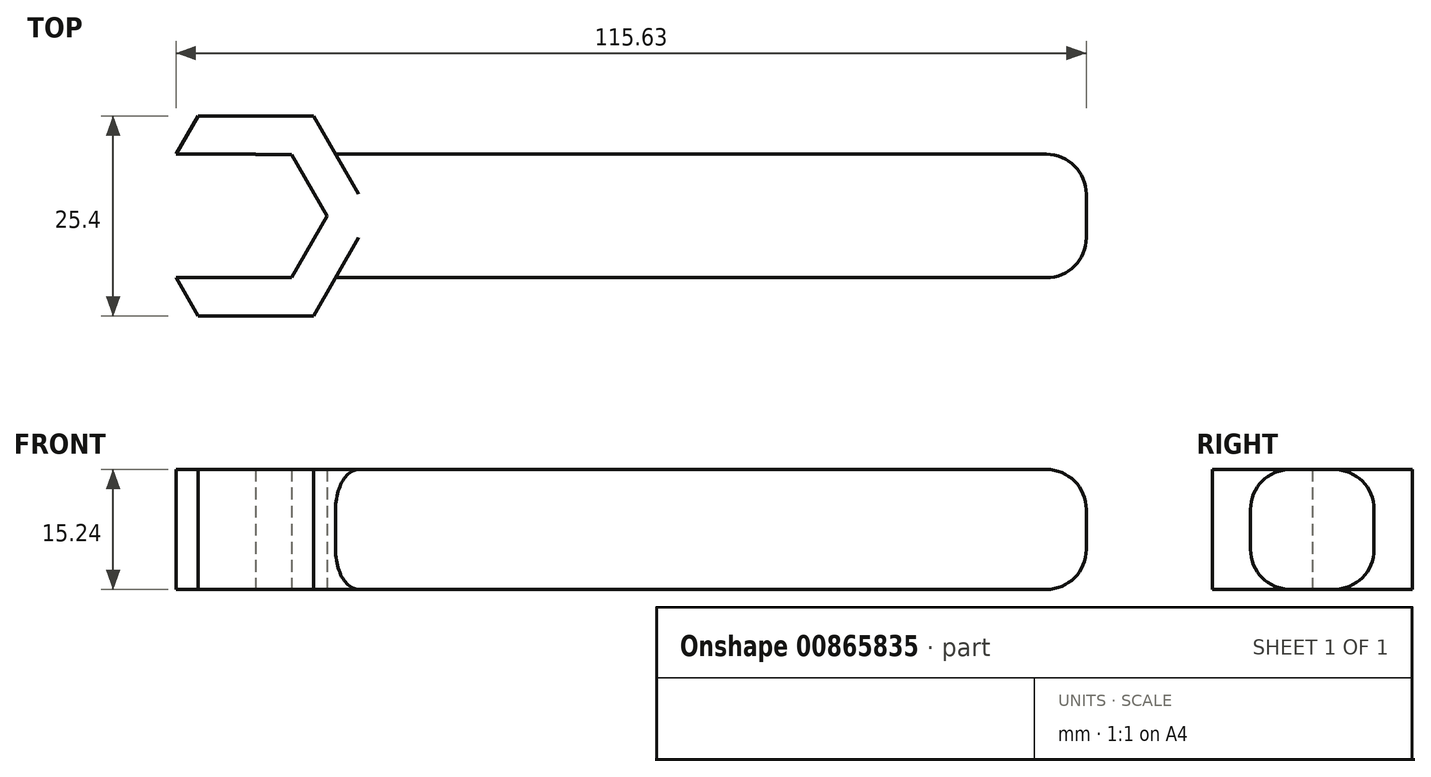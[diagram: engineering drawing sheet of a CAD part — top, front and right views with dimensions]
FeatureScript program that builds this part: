
annotation { "Feature Type Name" : "Feature", "Feature Type Description" : "" }
export const myFeature = defineFeature(function(context is Context, id is Id, definition is map)
    precondition{}
    {
        {
            var Q0;
            Q0=qCreatedBy(makeId("Top.planeOp"),FACE);
            var sketch = newSketch(context, id + "F0", { "sketchPlane" : qUnion([Q0])});
            skLineSegment(sketch, "E0.bottom", {"start": v(-35.06, 20.53) * mm, "end": v(70.43, 20.53) * mm});
            skLineSegment(sketch, "E0.top", {"start": v(-35.06, 4.85) * mm, "end": v(70.43, 4.85) * mm});
            skLineSegment(sketch, "E0.left", {"start": v(-35.06, 20.53) * mm, "end": v(-35.06, 4.85) * mm});
            skLineSegment(sketch, "E0.right", {"start": v(70.43, 20.53) * mm, "end": v(70.43, 4.85) * mm});
            skCircle(sketch, "E1.cCircle", {"center": v(-35.06, 12.69) * mm, "radius": 12.7 * mm, "construction": true});
            skLineSegment(sketch, "E1.0", {"start": v(-20.4, 12.69) * mm, "end": v(-27.73, 0) * mm});
            skLineSegment(sketch, "E1.1", {"start": v(-27.73, 0) * mm, "end": v(-42.4, 0) * mm});
            skLineSegment(sketch, "E1.2", {"start": v(-42.4, 0) * mm, "end": v(-49.73, 12.69) * mm});
            skLineSegment(sketch, "E1.3", {"start": v(-49.73, 12.69) * mm, "end": v(-42.4, 25.39) * mm});
            skLineSegment(sketch, "E1.4", {"start": v(-42.4, 25.39) * mm, "end": v(-27.73, 25.39) * mm});
            skLineSegment(sketch, "E1.5", {"start": v(-27.73, 25.39) * mm, "end": v(-20.4, 12.69) * mm});
            skPoint(sketch, "E1.0.midPoint", {"position": v(-24.07, 6.34) * mm});
            skCircle(sketch, "E2.cCircle", {"center": v(-35.06, 12.69) * mm, "radius": 7.83 * mm, "construction": true});
            skLineSegment(sketch, "E2.0", {"start": v(-39.58, 4.86) * mm, "end": v(-44.1, 12.69) * mm});
            skLineSegment(sketch, "E2.1", {"start": v(-44.1, 12.69) * mm, "end": v(-39.58, 20.52) * mm});
            skLineSegment(sketch, "E2.2", {"start": v(-39.58, 20.52) * mm, "end": v(-30.54, 20.52) * mm});
            skLineSegment(sketch, "E2.3", {"start": v(-30.54, 20.52) * mm, "end": v(-26.02, 12.69) * mm});
            skLineSegment(sketch, "E2.4", {"start": v(-26.02, 12.69) * mm, "end": v(-30.54, 4.86) * mm});
            skLineSegment(sketch, "E2.5", {"start": v(-30.54, 4.86) * mm, "end": v(-39.58, 4.86) * mm});
            skPoint(sketch, "E2.0.midPoint", {"position": v(-41.84, 8.78) * mm});
            skLineSegment(sketch, "E3.bottom", {"start": v(-35.06, 20.53) * mm, "end": v(-62.08, 20.53) * mm});
            skLineSegment(sketch, "E3.top", {"start": v(-35.06, 4.85) * mm, "end": v(-62.08, 4.85) * mm});
            skLineSegment(sketch, "E3.right", {"start": v(-62.08, 20.53) * mm, "end": v(-62.08, 4.85) * mm});
            skSolve(sketch);
        }
        {
            var Q0;
            {var subQ1=sQuery(id+"F0.wireOp",EDGE,"E1.4");Q0=makeQuery(id+"F0.imprint","IMPRINT",FACE,{"disambiguationData":[TD([[makeQuery(id+"F0.imprint","IMPRINT",EDGE,{"derivedFrom":subQ1}),-1.0]])]});}
            var Q1;
            {var subQ12=sQuery(id+"F0.wireOp",EDGE,"E2.3");Q1=makeQuery(id+"F0.imprint","IMPRINT",FACE,{"disambiguationData":[TD([[makeQuery(id+"F0.imprint","IMPRINT",EDGE,{"derivedFrom":subQ12}),1.0]])]});}
            var Q2;
            {var subQ1=sQuery(id+"F0.wireOp",EDGE,"E1.1");Q2=makeQuery(id+"F0.imprint","IMPRINT",FACE,{"disambiguationData":[TD([[makeQuery(id+"F0.imprint","IMPRINT",EDGE,{"derivedFrom":subQ1}),-1.0]])]});}
            var Q3;
            {var subQ5=sQuery(id+"F0.wireOp",EDGE,"E0.right");Q3=makeQuery(id+"F0.imprint","IMPRINT",FACE,{"disambiguationData":[TD([[makeQuery(id+"F0.imprint","IMPRINT",EDGE,{"derivedFrom":subQ5}),-1.0]])]});}
            extrude(context, id + "F1", {"entities" : qUnion([Q0, Q1, Q2, Q3]), "depth" : 15.24 * mm, "offsetDistance" : 25.4 * mm});
        }
        {
            var Q0;
            Q0=makeQuery(id+"F1.opExtrude","SWEPT_EDGE",EDGE,{"disambiguationData":[OSD([sQuery(id+"F0.wireOp",EDGE,"E0.bottom"),sQuery(id+"F0.wireOp",EDGE,"E0.right")])]});
            var Q1;
            Q1=makeQuery(id+"F1.opExtrude","CAP_EDGE",EDGE,{"disambiguationData":[OSD([sQuery(id+"F0.wireOp",EDGE,"E0.right")])],"isStart":false});
            fillet(context, id + "F2", {"entities" : qUnion([Q0, Q1]), "radius" : 5.08 * mm, "tangentPropagation" : true, "allowEdgeOverflow" : false});
        }
        {
            var Q0;
            Q0=makeQuery(id+"F1.opExtrude","CAP_EDGE",EDGE,{"disambiguationData":[OSD([sQuery(id+"F0.wireOp",EDGE,"E0.right")])],"isStart":true});
            fillet(context, id + "F3", {"entities" : qUnion([Q0]), "radius" : 5.08 * mm, "tangentPropagation" : true, "allowEdgeOverflow" : false});
        }
        {
            var Q0;
            Q0=makeQuery(id+"F1.opExtrude","SWEPT_EDGE",EDGE,{"disambiguationData":[OSD([sQuery(id+"F0.wireOp",EDGE,"E0.top"),sQuery(id+"F0.wireOp",EDGE,"E0.right")])]});
            fillet(context, id + "F4", {"entities" : qUnion([Q0]), "radius" : 5.08 * mm, "tangentPropagation" : true, "allowEdgeOverflow" : false});
        }
        {
            var Q0;
            {var subQ0=sQuery(id+"F0.wireOp",EDGE,"E0.right");Q0=makeQuery(id+"F2.opFillet","BLEND_EDGE",EDGE,{"blendedFrom":[makeQuery(id+"F1.opExtrude","SWEPT_EDGE",EDGE,{"disambiguationData":[OSD([sQuery(id+"F0.wireOp",EDGE,"E0.bottom"),subQ0])]}),makeQuery(id+"F1.opExtrude","CAP_EDGE",EDGE,{"disambiguationData":[OSD([subQ0])],"isStart":false})],"blendedInto":[]});}
            fillet(context, id + "F5", {"entities" : qUnion([Q0]), "radius" : 5.08 * mm, "tangentPropagation" : true, "allowEdgeOverflow" : false});
        }
    });
